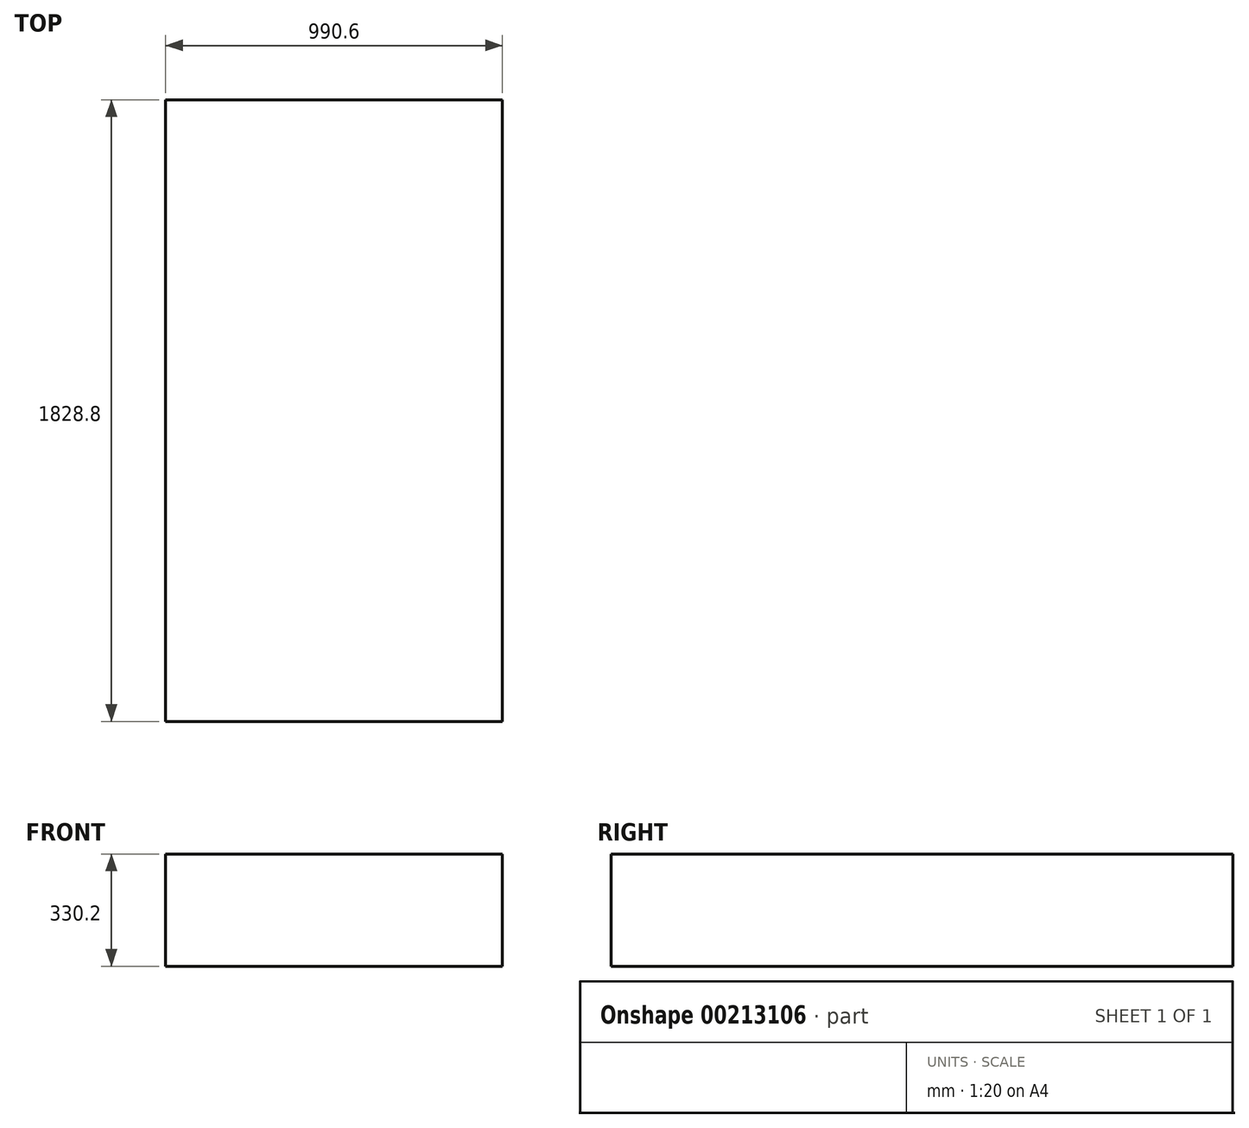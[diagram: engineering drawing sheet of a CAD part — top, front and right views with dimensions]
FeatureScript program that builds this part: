
annotation { "Feature Type Name" : "Feature", "Feature Type Description" : "" }
export const myFeature = defineFeature(function(context is Context, id is Id, definition is map)
    precondition{}
    {
        {
            var Q0;
            Q0=qCreatedBy(makeId("Front.planeOp"),FACE);
            var sketch = newSketch(context, id + "F0", { "sketchPlane" : qUnion([Q0])});
            skLineSegment(sketch, "E0.bottom", {"start": v(-35.67, 293.71) * mm, "end": v(954.93, 293.71) * mm});
            skLineSegment(sketch, "E0.top", {"start": v(-35.67, -36.49) * mm, "end": v(954.93, -36.49) * mm});
            skLineSegment(sketch, "E0.left", {"start": v(-35.67, 293.71) * mm, "end": v(-35.67, -36.49) * mm});
            skLineSegment(sketch, "E0.right", {"start": v(954.93, 293.71) * mm, "end": v(954.93, -36.49) * mm});
            skSolve(sketch);
        }
        {
            var Q0;
            Q0=makeQuery(id+"F0.imprint","IMPRINT",FACE,{"disambiguationData":[TD([[makeQuery(id+"F0.imprint","IMPRINT",EDGE,{"derivedFrom":sQuery(id+"F0.wireOp",EDGE,"E0.bottom")}),-1.0]])]});
            extrude(context, id + "F1", {"entities" : qUnion([Q0]), "depth" : 1828.8 * mm});
        }
    });
